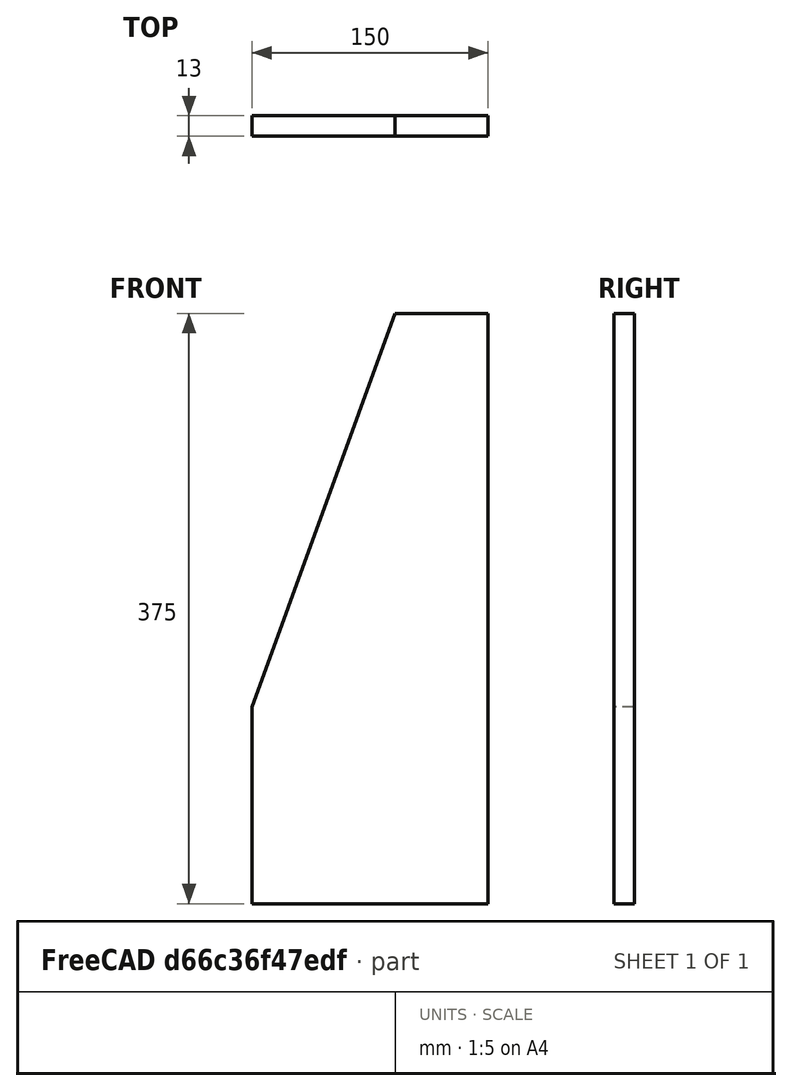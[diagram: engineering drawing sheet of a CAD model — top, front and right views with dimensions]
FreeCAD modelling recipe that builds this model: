
FCSTD DOCUMENT  (FreeCAD 0.18R14555 (Git shallow))
Label: 8050_Frame_Side
License: All rights reserved
LicenseURL: http://en.wikipedia.org/wiki/All_rights_reserved
objects: Sketcher::SketchObject×1, PartDesign::Pad×1, PartDesign::Body×1
note: 4 computed .brp shape members not serialized (recipe doc carries the construction recipe); baked Part::Feature solids carry a one-line shape summary decoded from their .brp

FEATURE [Sketcher::SketchObject] Sketch  label="SideWall"
  MapMode = 5
  Placement = pos=(0,0,0) rot=(1,0,0;1.5708rad)
  Support = -> [XZ_Plane]
  sketch-geometry (5):
    g0: LineSegment StartX=0 StartY=0 StartZ=0 EndX=150 EndY=0 EndZ=0
    g1: LineSegment StartX=150 StartY=0 StartZ=0 EndX=150 EndY=375 EndZ=0
    g2: LineSegment StartX=150 StartY=375 StartZ=0 EndX=90.9926 EndY=375 EndZ=0
    g3: LineSegment StartX=90.9926 StartY=375 StartZ=0 EndX=0 EndY=125 EndZ=0
    g4: LineSegment StartX=0 StartY=125 StartZ=0 EndX=0 EndY=0 EndZ=0
  constraints (14):
    c: Horizontal(g0)
    c: Vertical(g1)
    c: Coincident(g2,g1)
    c: Vertical(g4)
    c: Coincident(g2,g3)
    c: Angle(g3,g2) = 1.91986
    c: DistanceY(g4,g4) = 125
    c: Coincident(g0,g4)
    c: Perpendicular(g1,g2)
    c: DistanceY(g1,g1) = 375
    c: DistanceX(g0,g0) = 150
    c: Coincident(g3,g4)
    c: Coincident(g1,g0)
    c: Coincident(g-1,g0)
FEATURE [PartDesign::Pad] Pad
  Length = 13
  Length2 = 100
  Midplane = true
  Placement = pos=(0,0,0) rot=(1,0,0;1.5708rad)
  Profile = -> Sketch
  Type = 0
FEATURE [PartDesign::Body] Body
  Group = -> [Sketch,Pad]
  Origin = -> Origin
  Tip = -> Pad
